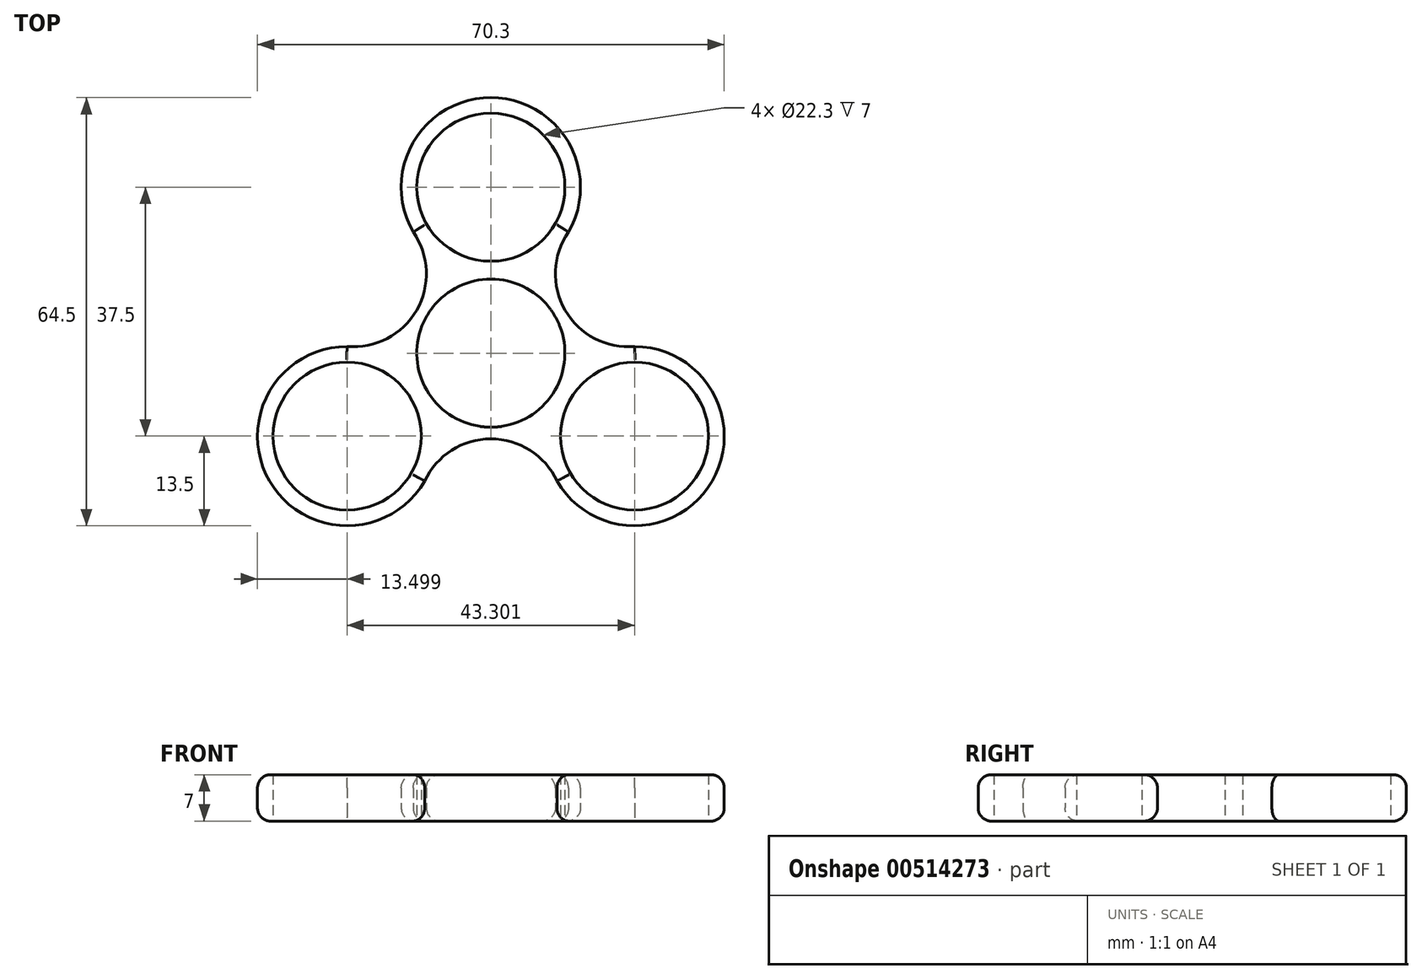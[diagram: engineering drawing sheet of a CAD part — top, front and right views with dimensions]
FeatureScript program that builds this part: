
annotation { "Feature Type Name" : "Feature", "Feature Type Description" : "" }
export const myFeature = defineFeature(function(context is Context, id is Id, definition is map)
    precondition{}
    {
        {
            var Q0;
            Q0=qCreatedBy(makeId("Top.planeOp"),FACE);
            var sketch = newSketch(context, id + "F0", { "sketchPlane" : qUnion([Q0])});
            skCircle(sketch, "E0", {"center": v(0, 0) * mm, "radius": 11.15 * mm});
            skCircle(sketch, "E1", {"center": v(0, 25) * mm, "radius": 11.15 * mm});
            skCircle(sketch, "E2", {"center": v(-21.65, -12.5) * mm, "radius": 11.15 * mm});
            skCircle(sketch, "E3", {"center": v(21.65, -12.5) * mm, "radius": 11.15 * mm});
            skCircle(sketch, "E4", {"center": v(21.65, -12.5) * mm, "radius": 13.5 * mm});
            skCircle(sketch, "E5", {"center": v(-21.65, -12.5) * mm, "radius": 13.5 * mm});
            skCircle(sketch, "E6", {"center": v(0, 25) * mm, "radius": 13.5 * mm});
            skArc(sketch, "E7", {"start": v(-21.65, 1) * mm, "mid": v(-11.19, 6.46) * mm, "end": v(-11.7, 18.25) * mm});
            skArc(sketch, "E8", {"start": v(11.7, 18.25) * mm, "mid": v(11.19, 6.46) * mm, "end": v(21.65, 1) * mm});
            skArc(sketch, "E9", {"start": v(9.96, -19.25) * mm, "mid": v(0, -12.92) * mm, "end": v(-9.96, -19.25) * mm});
            skSolve(sketch);
        }
        {
            var Q0;
            Q0=makeQuery(id+"F0.imprint","IMPRINT",FACE,{"disambiguationData":[TD([[makeQuery(id+"F0.imprint","IMPRINT",EDGE,{"derivedFrom":sQuery(id+"F0.wireOp",EDGE,"E1")}),-1.0]])]});
            var Q1;
            Q1=makeQuery(id+"F0.imprint","IMPRINT",FACE,{"disambiguationData":[TD([[makeQuery(id+"F0.imprint","IMPRINT",EDGE,{"derivedFrom":sQuery(id+"F0.wireOp",EDGE,"E0")}),-1.0]])]});
            var Q2;
            Q2=makeQuery(id+"F0.imprint","IMPRINT",FACE,{"disambiguationData":[TD([[makeQuery(id+"F0.imprint","IMPRINT",EDGE,{"derivedFrom":sQuery(id+"F0.wireOp",EDGE,"E3")}),-1.0]])]});
            var Q3;
            Q3=makeQuery(id+"F0.imprint","IMPRINT",FACE,{"disambiguationData":[TD([[makeQuery(id+"F0.imprint","IMPRINT",EDGE,{"derivedFrom":sQuery(id+"F0.wireOp",EDGE,"E2")}),-1.0]])]});
            extrude(context, id + "F1", {"entities" : qUnion([Q0, Q1, Q2, Q3]), "depth" : 7 * mm});
        }
        {
            var Q0;
            Q0=makeQuery(id+"F1.opExtrude","CAP_EDGE",EDGE,{"disambiguationData":[OSD([sQuery(id+"F0.wireOp",EDGE,"E6")])],"isStart":false});
            var Q1;
            Q1=makeQuery(id+"F1.opExtrude","CAP_EDGE",EDGE,{"disambiguationData":[OSD([sQuery(id+"F0.wireOp",EDGE,"E7")])],"isStart":false});
            var Q2;
            Q2=makeQuery(id+"F1.opExtrude","CAP_EDGE",EDGE,{"disambiguationData":[OSD([sQuery(id+"F0.wireOp",EDGE,"E5")])],"isStart":false});
            var Q3;
            Q3=makeQuery(id+"F1.opExtrude","CAP_EDGE",EDGE,{"disambiguationData":[OSD([sQuery(id+"F0.wireOp",EDGE,"E9")])],"isStart":false});
            var Q4;
            Q4=makeQuery(id+"F1.opExtrude","CAP_EDGE",EDGE,{"disambiguationData":[OSD([sQuery(id+"F0.wireOp",EDGE,"E4")])],"isStart":false});
            var Q5;
            Q5=makeQuery(id+"F1.opExtrude","CAP_EDGE",EDGE,{"disambiguationData":[OSD([sQuery(id+"F0.wireOp",EDGE,"E8")])],"isStart":false});
            var Q6;
            Q6=makeQuery(id+"F1.opExtrude","CAP_EDGE",EDGE,{"disambiguationData":[OSD([sQuery(id+"F0.wireOp",EDGE,"E6")])],"isStart":true});
            var Q7;
            Q7=makeQuery(id+"F1.opExtrude","CAP_EDGE",EDGE,{"disambiguationData":[OSD([sQuery(id+"F0.wireOp",EDGE,"E7")])],"isStart":true});
            var Q8;
            Q8=makeQuery(id+"F1.opExtrude","CAP_EDGE",EDGE,{"disambiguationData":[OSD([sQuery(id+"F0.wireOp",EDGE,"E5")])],"isStart":true});
            var Q9;
            Q9=makeQuery(id+"F1.opExtrude","CAP_EDGE",EDGE,{"disambiguationData":[OSD([sQuery(id+"F0.wireOp",EDGE,"E9")])],"isStart":true});
            var Q10;
            Q10=makeQuery(id+"F1.opExtrude","CAP_EDGE",EDGE,{"disambiguationData":[OSD([sQuery(id+"F0.wireOp",EDGE,"E4")])],"isStart":true});
            var Q11;
            Q11=makeQuery(id+"F1.opExtrude","CAP_EDGE",EDGE,{"disambiguationData":[OSD([sQuery(id+"F0.wireOp",EDGE,"E8")])],"isStart":true});
            fillet(context, id + "F2", {"entities" : qUnion([Q0, Q1, Q2, Q3, Q4, Q5, Q6, Q7, Q8, Q9, Q10, Q11]), "radius" : 2 * mm, "tangentPropagation" : true, "allowEdgeOverflow" : false});
        }
    });
